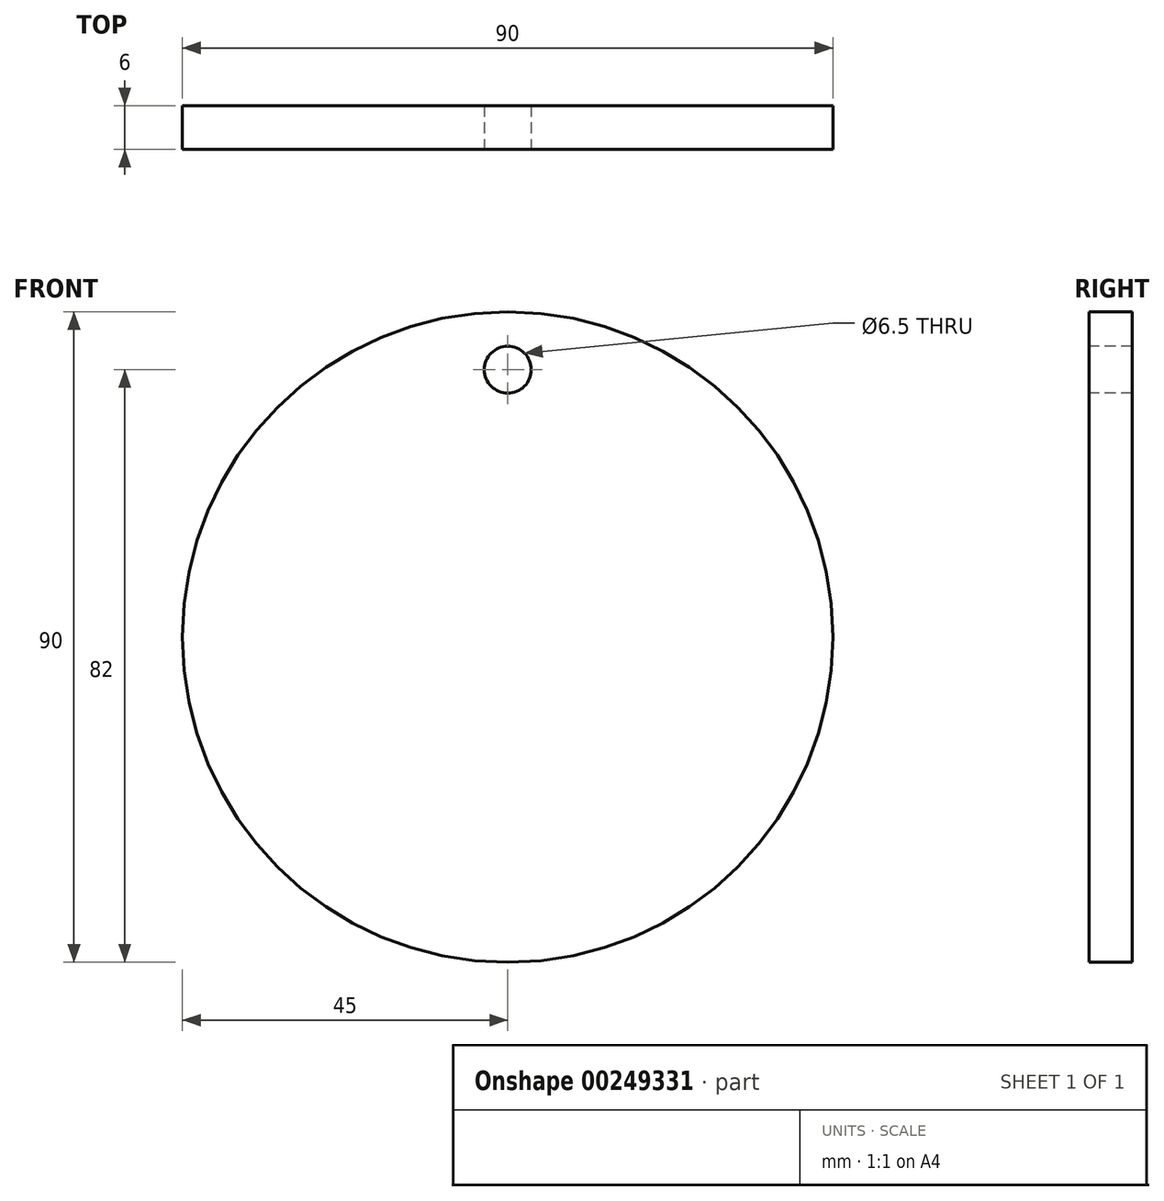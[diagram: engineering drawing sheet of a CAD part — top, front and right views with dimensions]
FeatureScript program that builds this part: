
annotation { "Feature Type Name" : "Feature", "Feature Type Description" : "" }
export const myFeature = defineFeature(function(context is Context, id is Id, definition is map)
    precondition{}
    {
        {
            var Q0;
            Q0=qCreatedBy(makeId("Front.planeOp"),FACE);
            var sketch = newSketch(context, id + "F0", { "sketchPlane" : qUnion([Q0])});
            skCircle(sketch, "E0", {"center": v(0, 0) * mm, "radius": 45 * mm});
            skSolve(sketch);
        }
        {
            var Q0;
            Q0=makeQuery(id+"F0.imprint","IMPRINT",FACE,{"disambiguationData":[TD([[makeQuery(id+"F0.imprint","IMPRINT",EDGE,{"derivedFrom":sQuery(id+"F0.wireOp",EDGE,"E0")}),1.0]])]});
            extrude(context, id + "F1", {"entities" : qUnion([Q0]), "depth" : 6 * mm, "symmetric" : true});
        }
        {
            var Q0;
            Q0=makeQuery(id+"F1.opExtrude","CAP_FACE",FACE,{"disambiguationData":[OSD([sQuery(id+"F0.wireOp",EDGE,"E0"),sQuery(id+"F0.wireOp",EDGE,"4IDOolbJ-IXsx-Q9G2-orr8-6GJYecRueEph")])],"isStart":false});
            var sketch = newSketch(context, id + "F2", { "sketchPlane" : qUnion([Q0])});
            skCircle(sketch, "E1", {"center": v(0, 37) * mm, "radius": 3.25 * mm});
            skSolve(sketch);
        }
        {
            var Q0;
            Q0=makeQuery(id+"F2.imprint","IMPRINT",FACE,{"disambiguationData":[TD([[makeQuery(id+"F2.imprint","IMPRINT",EDGE,{"derivedFrom":sQuery(id+"F2.wireOp",EDGE,"E1")}),1.0]])]});
            extrude(context, id + "F3", {"entities" : qUnion([Q0]), "operationType" : NewBodyOperationType.REMOVE, "oppositeDirection" : true, "depth" : 25 * mm});
        }
    });
